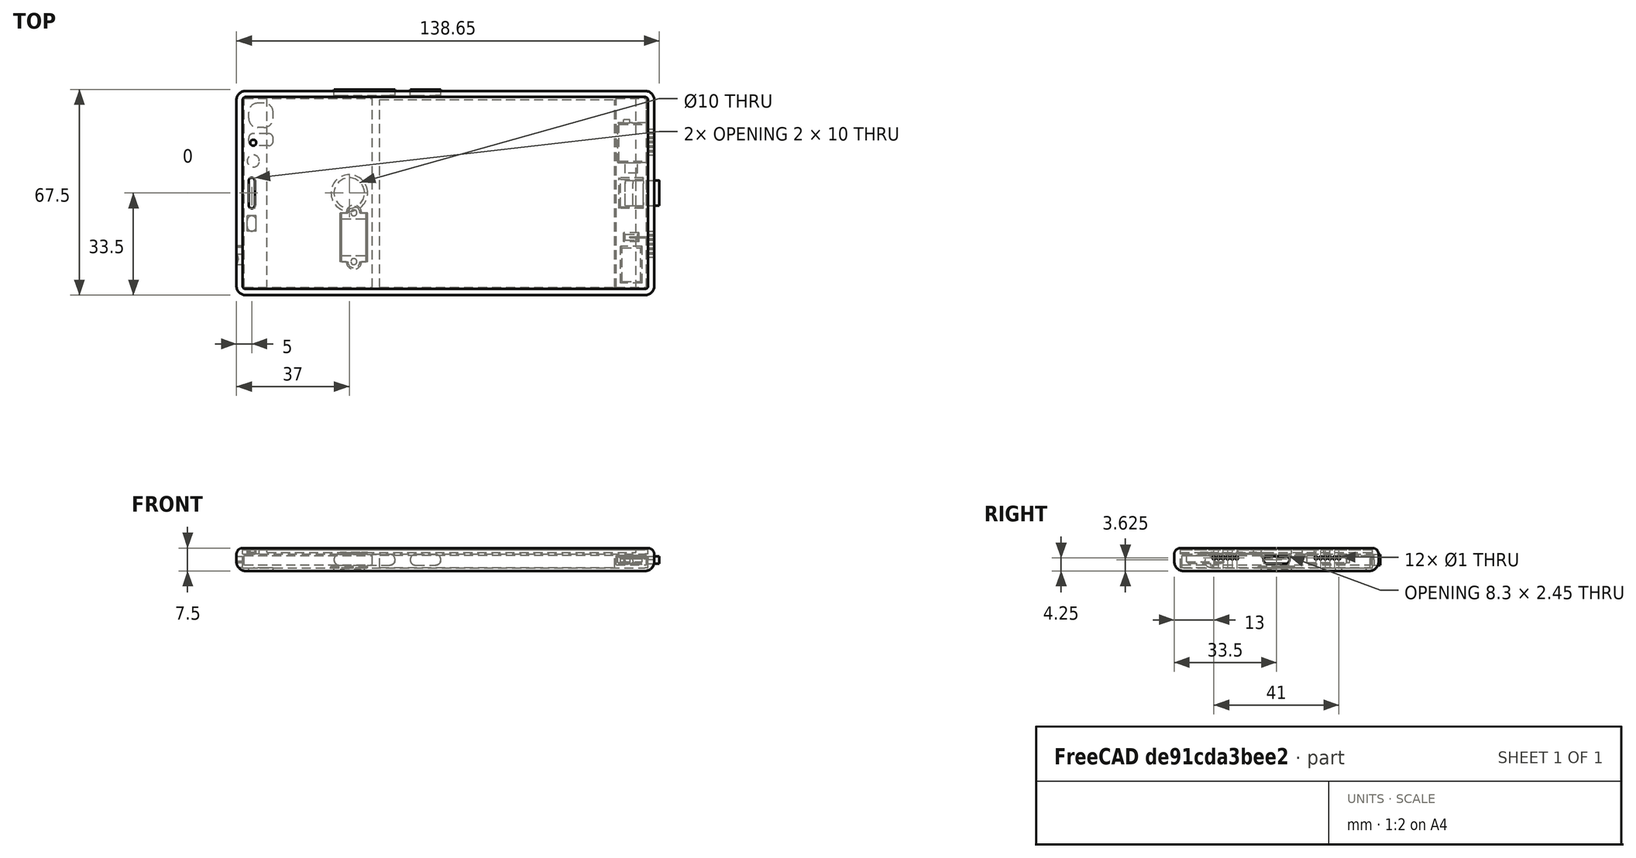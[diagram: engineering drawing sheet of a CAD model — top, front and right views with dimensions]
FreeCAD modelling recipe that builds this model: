
FCSTD DOCUMENT  (FreeCAD 0.16R6706 (Git))
Label: uCromy 2017
License: All rights reserved
LicenseURL: http://en.wikipedia.org/wiki/All_rights_reserved
objects: Part::Cut×45, Part::Box×37, Part::Cylinder×31, Part::Fillet×22, Part::MultiFuse×12, Part::Chamfer×4, Part::Sphere×1
note: 152 computed .brp shape members not serialized (recipe doc carries the construction recipe); baked Part::Feature solids carry a one-line shape summary decoded from their .brp

FEATURE [Part::Box] Box  label="Cubo"
  Height = 7.5
  Length = 137
  Width = 67
FEATURE [Part::Fillet] Fillet
  Base = -> Box
  Edges = 8 edges r=3: [Edge1,Edge3,Edge4,Edge5,Edge7,Edge8,Edge9,Edge11]
FEATURE [Part::Fillet] Fillet001
  Base = -> Fillet
  Edges = 7 edges r=2: [Edge1,Edge5,Edge7,Edge8,Edge9,Edge10,Edge11]
FEATURE [Part::Box] Box001  label="Cubo001"
  Height = 10
  Length = 133
  Placement = pos=(2,2,5.5) rot=(0,0,1;0rad)
  Width = 63
FEATURE [Part::Fillet] Fillet002
  Base = -> Box001
  Edges = 4 edges r=1: [Edge1,Edge3,Edge5,Edge7]
  Placement = pos=(0,0,-4.5) rot=(0,0,1;0rad)
FEATURE [Part::Cut] Cut  label="Chassis"
  Base = -> Fillet001
  Tool = -> Fillet002
FEATURE [Part::Box] Box003  label="Cubo003"
  Height = 0.5
  Length = 133
  Placement = pos=(2,2,5.5) rot=(0,0,1;0rad)
  Width = 63
FEATURE [Part::Fillet] Fillet004  label="Dont show001"
  Base = -> Box003
  Edges = 4 edges r=1: [Edge1,Edge3,Edge5,Edge7]
FEATURE [Part::Box] Box004  label="Cubo004"
  Height = 0.5
  Length = 133
  Placement = pos=(2,2,5.5) rot=(0,0,1;0rad)
  Width = 63
FEATURE [Part::Fillet] Fillet005  label="Touchscreen"
  Base = -> Box004
  Edges = 4 edges r=1: [Edge1,Edge3,Edge5,Edge7]
  Placement = pos=(0,0,1.5) rot=(0,0,1;0rad)
FEATURE [Part::Box] Box005  label="Screen"
  Height = 1
  Length = 121
  Placement = pos=(10,2,6) rot=(0,0,1;0rad)
  Width = 63
FEATURE [Part::Box] Box006  label="Screen001"
  Height = 1
  Length = 8
  Placement = pos=(2,2,6) rot=(0,0,1;0rad)
  Width = 63
FEATURE [Part::Box] Box007  label="Screen002"
  Height = 1
  Length = 4
  Placement = pos=(131,2,6) rot=(0,0,1;0rad)
  Width = 63
FEATURE [Part::Fillet] Fillet006  label="Bottom"
  Base = -> Box007
  Edges = 2 edges r=1: [Edge5,Edge7]
FEATURE [Part::Fillet] Fillet007  label="Top"
  Base = -> Box006
  Edges = 2 edges r=1: [Edge1,Edge3]
FEATURE [Part::Box] Box008  label="Cubo005"
  Height = 0.2
  Length = 8
  Placement = pos=(35,10.5,1) rot=(0,0,1;0rad)
  Width = 16
FEATURE [Part::Cylinder] Cylinder  label="Cilindro"
  Angle = 360
  Height = 0.2
  Placement = pos=(39,10.5,1) rot=(0,0,1;0rad)
  Radius = 2
FEATURE [Part::Cylinder] Cylinder001  label="Cilindro001"
  Angle = 360
  Height = 0.2
  Placement = pos=(39,26.5,1) rot=(0,0,1;0rad)
  Radius = 2
FEATURE [Part::MultiFuse] Fusion  label="Chapa flex pantalla"
  Placement = pos=(-0.5,0.5,4.8) rot=(0,0,1;0rad)
  Shapes = -> [Box008,Cylinder001,Cylinder]
FEATURE [Part::Box] Box009  label="Cubo006"
  Height = 0.3
  Length = 9
  Placement = pos=(34,11,1) rot=(0,0,1;0rad)
  Width = 16
FEATURE [Part::Cylinder] Cylinder002  label="Cilindro002"
  Angle = 360
  Height = 0.3
  Placement = pos=(38.5,11,1) rot=(0,0,1;0rad)
  Radius = 2.5
FEATURE [Part::Cylinder] Cylinder003  label="Cilindro003"
  Angle = 360
  Height = 0.3
  Placement = pos=(38.5,27,1) rot=(0,0,1;0rad)
  Radius = 2.5
FEATURE [Part::MultiFuse] Fusion001  label="Agujero flex pantalla"
  Placement = pos=(0,0,4.4) rot=(0,0,1;0rad)
  Shapes = -> [Box009,Cylinder003,Cylinder002]
FEATURE [Part::Box] Box010  label="Cubo007"
  Height = 1.2
  Length = 8
  Placement = pos=(34.5,11,5) rot=(0,0,1;0rad)
  Width = 16
FEATURE [Part::Cylinder] Cylinder004  label="Cilindro004"
  Angle = 360
  Height = 10
  Placement = pos=(38.5,27,1) rot=(0,0,1;0rad)
  Radius = 1
FEATURE [Part::Cylinder] Cylinder005  label="Cilindro005"
  Angle = 360
  Height = 10
  Placement = pos=(38.5,11,1) rot=(0,0,1;0rad)
  Radius = 1
FEATURE [Part::Cut] Cut001
  Base = -> Box010
  Tool = -> Cylinder004
FEATURE [Part::Cut] Cut002
  Base = -> Cut001
  Tool = -> Cylinder005
FEATURE [Part::Cut] Cut003
  Base = -> Fusion001
  Tool = -> Cylinder005
FEATURE [Part::Cut] Cut004
  Base = -> Cut003
  Placement = pos=(0,0,0.4) rot=(0,0,1;0rad)
  Tool = -> Cylinder004
FEATURE [Part::Cut] Cut005
  Base = -> Fusion
  Tool = -> Cylinder004
FEATURE [Part::Cut] Cut006  label="Chapa flex"
  Base = -> Cut005
  Tool = -> Cylinder005
FEATURE [Part::Cylinder] Cylinder006  label="Cilindro006"
  Angle = 360
  Height = 10
  Placement = pos=(38.5,11,1) rot=(0,0,1;0rad)
  Radius = 1.5
FEATURE [Part::Cylinder] Cylinder007  label="Cilindro007"
  Angle = 360
  Height = 10
  Placement = pos=(38.5,27,1) rot=(0,0,1;0rad)
  Radius = 1.5
FEATURE [Part::Cut] Cut007
  Base = -> Cut002
  Tool = -> Cylinder007
FEATURE [Part::Cut] Cut008
  Base = -> Cut007
  Tool = -> Cylinder006
FEATURE [Part::MultiFuse] Fusion002  label="Dont show"
  Shapes = -> [Cut004,Cut008]
FEATURE [Part::Cut] Cut009
  Base = -> Fillet004
  Tool = -> Fusion002
FEATURE [Part::Box] Box011  label="Cubo008"
  Height = 0.3
  Length = 9
  Placement = pos=(34,11,5.5) rot=(0,0,1;0rad)
  Width = 2
FEATURE [Part::Box] Box012  label="Cubo009"
  Height = 0.3
  Length = 9
  Placement = pos=(34,25,5.5) rot=(0,0,1;0rad)
  Width = 2
FEATURE [Part::MultiFuse] Fusion003
  Shapes = -> [Cut009,Box011,Box012]
FEATURE [Part::Cylinder] Cylinder008  label="Cilindro008"
  Angle = 360
  Height = 0.1
  Placement = pos=(38.5,11,1) rot=(0,0,1;0rad)
  Radius = 1.2
FEATURE [Part::Cylinder] Cylinder009  label="Cilindro009"
  Angle = 360
  Height = 0.1
  Placement = pos=(38.5,27,1) rot=(0,0,1;0rad)
  Radius = 1.2
FEATURE [Part::Cut] Cut010
  Base = -> Fusion003
  Tool = -> Cylinder008
FEATURE [Part::Cut] Cut011
  Base = -> Cut010
  Tool = -> Cylinder009
FEATURE [Part::Cut] Cut012
  Base = -> Cut011
  Tool = -> Cylinder004
FEATURE [Part::Cut] Cut013
  Base = -> Cut012
  Tool = -> Cylinder005
FEATURE [Part::Box] Box013  label="PCB"
  Height = 3
  Length = 42
  Placement = pos=(2.5,2.5,2) rot=(0,0,1;0rad)
  Width = 62
FEATURE [Part::Box] Box014  label="Loud_Speaker"
  Height = 3
  Length = 10
  Placement = pos=(124.5,2.5,2) rot=(0,0,1;0rad)
  Width = 62
FEATURE [Part::Box] Box015  label="Battery"
  Height = 4.05
  Length = 77
  Placement = pos=(47,2.5,1.1) rot=(0,0,1;0rad)
  Width = 61.7
FEATURE [Part::Box] Box016  label="Cubo010"
  Height = 10
  Length = 2
  Placement = pos=(4,28.5,0) rot=(0,0,1;0rad)
  Width = 10
FEATURE [Part::Fillet] Fillet008
  Base = -> Box016
  Edges = 4 edges r=0.95: [Edge1,Edge3,Edge5,Edge7]
FEATURE [Part::Cut] Cut014
  Base = -> Fillet005
  Tool = -> Fillet008
FEATURE [Part::Cut] Cut015
  Base = -> Fillet007
  Tool = -> Fillet008
FEATURE [Part::Cylinder] Cylinder010  label="Cilindro010"
  Angle = 360
  Height = 10
  Placement = pos=(5.5,50,0) rot=(0,0,1;0rad)
  Radius = 1
FEATURE [Part::Cut] Cut016
  Base = -> Cut014
  Tool = -> Cylinder010
FEATURE [Part::Cut] Cut017
  Base = -> Cut013
  Tool = -> Cylinder010
FEATURE [Part::Cylinder] Cylinder011  label="Cilindro011"
  Angle = 360
  Height = 10
  Placement = pos=(5.5,44,0) rot=(0,0,1;0rad)
  Radius = 2
FEATURE [Part::Box] Box017  label="Cubo011"
  Height = 10
  Length = 3
  Placement = pos=(3.5,21,0) rot=(0,0,1;0rad)
  Width = 5
FEATURE [Part::Cylinder] Cylinder012  label="Cilindro012"
  Angle = 360
  Height = 2
  Placement = pos=(5.5,50,5.5) rot=(0,0,1;0rad)
  Radius = 1
FEATURE [Part::Cut] Cut018
  Base = -> Cut015
  Tool = -> Cylinder010
FEATURE [Part::Cut] Cut019
  Base = -> Cut017
  Tool = -> Cylinder011
FEATURE [Part::Cut] Cut020
  Base = -> Cut019
  Tool = -> Box017
FEATURE [Part::Box] Box018  label="Cubo012"
  Height = 10
  Length = 3
  Placement = pos=(3.5,21,0) rot=(0,0,1;0rad)
  Width = 5
FEATURE [Part::Fillet] Fillet009
  Base = -> Box018
  Edges = 4 edges r=1.49: [Edge1,Edge3,Edge5,Edge7]
FEATURE [Part::Cut] Cut021
  Base = -> Cut018
  Tool = -> Fillet009
FEATURE [Part::Cut] Cut022
  Base = -> Cut020
  Tool = -> Fillet008
FEATURE [Part::Cut] Cut023
  Base = -> Cut021
  Tool = -> Cylinder011
FEATURE [Part::Box] Box019  label="Cubo013"
  Height = 10
  Length = 8
  Placement = pos=(4,55,-1) rot=(0,0,1;0rad)
  Width = 8
FEATURE [Part::Fillet] Fillet010
  Base = -> Box019
  Edges = 4 edges r=3: [Edge1,Edge3,Edge5,Edge7]
FEATURE [Part::Box] Box020  label="Cubo014"
  Height = 1
  Length = 8
  Placement = pos=(4,55,-1) rot=(0,0,1;0rad)
  Width = 8
FEATURE [Part::Fillet] Fillet011  label="Lente Cámara"
  Base = -> Box020
  Edges = 4 edges r=3: [Edge1,Edge3,Edge5,Edge7]
  Placement = pos=(0,0,1) rot=(0,0,1;0rad)
FEATURE [Part::Box] Box021  label="Cubo015"
  Height = 10
  Length = 8
  Placement = pos=(4,55,-1) rot=(0,0,1;0rad)
  Width = 4
FEATURE [Part::Fillet] Fillet012
  Base = -> Box021
  Edges = 4 edges r=1.5: [Edge1,Edge3,Edge5,Edge7]
  Placement = pos=(0,-6,0) rot=(0,0,1;0rad)
FEATURE [Part::Cut] Cut024
  Base = -> Cut
  Tool = -> Fillet010
FEATURE [Part::Box] Box022  label="Cubo016"
  Height = 1
  Length = 8
  Placement = pos=(4,55,-1) rot=(0,0,1;0rad)
  Width = 4
FEATURE [Part::Fillet] Fillet013  label="Lente Flash"
  Base = -> Box022
  Edges = 4 edges r=1.5: [Edge1,Edge3,Edge5,Edge7]
  Placement = pos=(0,-6,1) rot=(0,0,1;0rad)
FEATURE [Part::Cut] Cut025
  Base = -> Cut024
  Tool = -> Fillet012
FEATURE [Part::MultiFuse] Fusion004
  Shapes = -> [Cut023,Cut022,Fillet006]
FEATURE [Part::Cylinder] Cylinder013  label="Cilindro013"
  Angle = 360
  Height = 10
  Placement = pos=(130,54,4.25) rot=(0.57735,0.57735,0.57735;2.0944rad)
  Radius = 0.5
FEATURE [Part::Cylinder] Cylinder014  label="Cilindro014"
  Angle = 360
  Height = 10
  Placement = pos=(130,51,4.25) rot=(0.57735,0.57735,0.57735;2.0944rad)
  Radius = 0.5
FEATURE [Part::Cylinder] Cylinder015  label="Cilindro015"
  Angle = 360
  Height = 10
  Placement = pos=(130,52.5,4.25) rot=(0.57735,0.57735,0.57735;2.0944rad)
  Radius = 0.5
FEATURE [Part::MultiFuse] Fusion005
  Shapes = -> [Cylinder013,Cylinder015,Cylinder014]
FEATURE [Part::Cylinder] Cylinder016  label="Cilindro016"
  Angle = 360
  Height = 10
  Placement = pos=(130,54,4.25) rot=(0.57735,0.57735,0.57735;2.0944rad)
  Radius = 0.5
FEATURE [Part::Cylinder] Cylinder017  label="Cilindro017"
  Angle = 360
  Height = 10
  Placement = pos=(130,51,4.25) rot=(0.57735,0.57735,0.57735;2.0944rad)
  Radius = 0.5
FEATURE [Part::Cylinder] Cylinder018  label="Cilindro018"
  Angle = 360
  Height = 10
  Placement = pos=(130,52.5,4.25) rot=(0.57735,0.57735,0.57735;2.0944rad)
  Radius = 0.5
FEATURE [Part::MultiFuse] Fusion006
  Placement = pos=(0,-4.5,0) rot=(0,0,1;0rad)
  Shapes = -> [Cylinder016,Cylinder018,Cylinder017]
FEATURE [Part::MultiFuse] Fusion007  label="Agujero altavoz"
  Shapes = -> [Fusion005,Fusion006]
FEATURE [Part::Cylinder] Cylinder021  label="Cilindro021"
  Angle = 360
  Height = 10
  Placement = pos=(130,52.5,4.25) rot=(0.57735,0.57735,0.57735;2.0944rad)
  Radius = 0.5
FEATURE [Part::Cylinder] Cylinder020  label="Cilindro020"
  Angle = 360
  Height = 10
  Placement = pos=(130,51,4.25) rot=(0.57735,0.57735,0.57735;2.0944rad)
  Radius = 0.5
FEATURE [Part::Cylinder] Cylinder019  label="Cilindro019"
  Angle = 360
  Height = 10
  Placement = pos=(130,54,4.25) rot=(0.57735,0.57735,0.57735;2.0944rad)
  Radius = 0.5
FEATURE [Part::MultiFuse] Fusion008  label="Fusion007"
  Placement = pos=(0,-38,0) rot=(0,0,1;0rad)
  Shapes = -> [Cylinder019,Cylinder021,Cylinder020]
FEATURE [Part::Cylinder] Cylinder022  label="Cilindro022"
  Angle = 360
  Height = 10
  Placement = pos=(130,52.5,4.25) rot=(0.57735,0.57735,0.57735;2.0944rad)
  Radius = 0.5
FEATURE [Part::Cylinder] Cylinder023  label="Cilindro023"
  Angle = 360
  Height = 10
  Placement = pos=(130,51,4.25) rot=(0.57735,0.57735,0.57735;2.0944rad)
  Radius = 0.5
FEATURE [Part::Cylinder] Cylinder024  label="Cilindro024"
  Angle = 360
  Height = 10
  Placement = pos=(130,54,4.25) rot=(0.57735,0.57735,0.57735;2.0944rad)
  Radius = 0.5
FEATURE [Part::MultiFuse] Fusion009  label="Fusion008"
  Placement = pos=(0,-33.5,0) rot=(0,0,1;0rad)
  Shapes = -> [Cylinder024,Cylinder022,Cylinder023]
FEATURE [Part::MultiFuse] Fusion010  label="Agujero Micro"
  Shapes = -> [Fusion008,Fusion009]
FEATURE [Part::Cut] Cut026
  Base = -> Cut025
  Tool = -> Fusion007
FEATURE [Part::Cut] Cut027
  Base = -> Cut026
  Tool = -> Fusion010
FEATURE [Part::Box] Box023  label="Cubo017"
  Height = 2.45
  Length = 6.65
  Width = 8.3
FEATURE [Part::Fillet] Fillet014  label="USB-C"
  Base = -> Box023
  Edges = 4 edges r=1: [Edge9,Edge10,Edge11,Edge12]
  Placement = pos=(132,29.35,2.4) rot=(0,0,1;0rad)
FEATURE [Part::Cut] Cut028
  Base = -> Cut027
  Tool = -> Fillet014
FEATURE [Part::Box] Box024  label="Cubo018"
  Height = 2.45
  Length = 8.65
  Width = 8.3
FEATURE [Part::Fillet] Fillet015  label="USB-C001"
  Base = -> Box024
  Edges = 4 edges r=1: [Edge9,Edge10,Edge11,Edge12]
  Placement = pos=(130,29.35,2.4) rot=(0,0,1;0rad)
FEATURE [Part::Cylinder] Cylinder026  label="phones"
  Angle = 360
  Height = 10
  Placement = pos=(-2,11.75,3) rot=(0.57735,0.57735,0.57735;2.0944rad)
  Radius = 1.75
FEATURE [Part::Cut] Cut029
  Base = -> Cut028
  Tool = -> Cylinder026
FEATURE [Part::Box] Box026  label="Agujero Altavoz"
  Height = 3
  Length = 10
  Placement = pos=(125,43.5,2.2) rot=(0,0,1;0rad)
  Width = 13
FEATURE [Part::Cut] Cut030
  Base = -> Box014
  Tool = -> Box026
FEATURE [Part::Cylinder] Cylinder027  label="Cilindro025"
  Angle = 360
  Height = 10
  Placement = pos=(0,16,3) rot=(0.57735,0.57735,0.57735;2.0944rad)
  Radius = 0.25
FEATURE [Part::Cylinder] Cylinder028  label="Cilindro026"
  Angle = 360
  Height = 10
  Placement = pos=(129,19,4.25) rot=(0.57735,0.57735,0.57735;2.0944rad)
  Radius = 0.25
FEATURE [Part::Cut] Cut031
  Base = -> Cut029
  Tool = -> Cylinder027
FEATURE [Part::Cut] Cut032
  Base = -> Cut030
  Tool = -> Cylinder028
FEATURE [Part::Box] Box027  label="Cubo021"
  Height = 2.45
  Length = 8.65
  Width = 8.3
FEATURE [Part::Fillet] Fillet016  label="USB-C002"
  Base = -> Box027
  Edges = 4 edges r=1: [Edge9,Edge10,Edge11,Edge12]
  Placement = pos=(127.5,29.35,2.4) rot=(0,0,1;0rad)
FEATURE [Part::Cut] Cut033
  Base = -> Cut032
  Tool = -> Fillet015
FEATURE [Part::Cylinder] Cylinder029  label="Cilindro027"
  Angle = 360
  Height = 10
  Placement = pos=(37,33.5,-1) rot=(0,0,1;0rad)
  Radius = 5
FEATURE [Part::Cylinder] Cylinder030  label="Cilindro028"
  Angle = 360
  Height = 1
  Placement = pos=(37,33.5,0) rot=(0,0,1;0rad)
  Radius = 5
FEATURE [Part::Cut] Cut034
  Base = -> Cut031
  Tool = -> Cylinder029
FEATURE [Part::Cylinder] Cylinder031  label="Cilindro029"
  Angle = 360
  Height = 0.5
  Placement = pos=(37,33.5,1) rot=(0,0,1;0rad)
  Radius = 6
FEATURE [Part::Sphere] Sphere  label="Esfera"
  Angle1 = 70
  Angle2 = 90
  Angle3 = 360
  Placement = pos=(37,33.5,-14.25) rot=(0,0,1;0rad)
  Radius = 15
FEATURE [Part::Cut] Cut035
  Base = -> Cylinder030
  Tool = -> Sphere
FEATURE [Part::Fillet] Fillet017
  Base = -> Cut035
  Edges = 1 edges: [Edge4 r1=1 r2=2]
FEATURE [Part::MultiFuse] Fusion011  label="Sensor de huellas"
  Shapes = -> [Fillet017,Cylinder031]
FEATURE [Part::Box] Box028  label="Cubo022"
  Height = 3.5
  Length = 10
  Placement = pos=(57,60,2.5) rot=(0,0,1;0rad)
  Width = 10
FEATURE [Part::Fillet] Fillet018
  Base = -> Box028
  Edges = 4 edges r=1.7: [Edge2,Edge4,Edge6,Edge8]
  Placement = pos=(0,0,-0.6) rot=(0,0,1;0rad)
FEATURE [Part::Box] Box029  label="Cubo023"
  Height = 3.5
  Length = 20
  Placement = pos=(57,60,2.5) rot=(0,0,1;0rad)
  Width = 10
FEATURE [Part::Fillet] Fillet019
  Base = -> Box029
  Edges = 4 edges r=1.7: [Edge2,Edge4,Edge6,Edge8]
  Placement = pos=(-25,0,-0.6) rot=(0,0,1;0rad)
FEATURE [Part::Box] Box030  label="Cubo024"
  Height = 3.5
  Length = 10
  Placement = pos=(57,60,2.5) rot=(0,0,1;0rad)
  Width = 2
FEATURE [Part::Fillet] Fillet020  label="PowerButton"
  Base = -> Box030
  Edges = 4 edges r=1.7: [Edge2,Edge4,Edge6,Edge8]
  Placement = pos=(0,5.5,-0.6) rot=(0,0,1;0rad)
FEATURE [Part::Box] Box031  label="Cubo025"
  Height = 3.5
  Length = 20
  Placement = pos=(57,60,2.5) rot=(0,0,1;0rad)
  Width = 2
FEATURE [Part::Fillet] Fillet021  label="VolumeButton"
  Base = -> Box031
  Edges = 4 edges r=1.7: [Edge2,Edge4,Edge6,Edge8]
  Placement = pos=(-25,5.5,-0.6) rot=(0,0,1;0rad)
FEATURE [Part::Cut] Cut036
  Base = -> Cut034
  Tool = -> Fillet019
FEATURE [Part::Cut] Cut037
  Base = -> Cut036
  Tool = -> Fillet018
FEATURE [Part::Box] Box032  label="Cubo026"
  Height = 10
  Length = 5
  Placement = pos=(124,14,0) rot=(0,0,1;0rad)
  Width = 3
FEATURE [Part::Chamfer] Chamfer
  Base = -> Box032
  Edges = 4 edges r=0.5: [Edge4,Edge8,Edge9,Edge11]
  Placement = pos=(3,3.5,4.2) rot=(0,0,1;0rad)
FEATURE [Part::Cut] Cut038
  Base = -> Cut033
  Tool = -> Chamfer
FEATURE [Part::Box] Box033  label="Cubo027"
  Height = 10
  Length = 8
  Placement = pos=(124,28.5,0) rot=(0,0,1;0rad)
  Width = 10
FEATURE [Part::Chamfer] Chamfer001
  Base = -> Box033
  Edges = 4 edges r=0.5: [Edge4,Edge8,Edge9,Edge11]
  Placement = pos=(1.5,0,4) rot=(0,0,1;0rad)
FEATURE [Part::Cut] Cut039
  Base = -> Cut038
  Tool = -> Chamfer001
FEATURE [Part::Box] Box034  label="Cubo028"
  Height = 3
  Length = 7
  Placement = pos=(126,4,2.5) rot=(0,0,1;0rad)
  Width = 12
FEATURE [Part::Chamfer] Chamfer002
  Base = -> Box034
  Edges = 4 edges r=0.5: [Edge4,Edge8,Edge9,Edge11]
FEATURE [Part::Cut] Cut040
  Base = -> Cut039
  Tool = -> Chamfer002
FEATURE [Part::Box] Box035  label="Cubo029"
  Height = 2.45
  Length = 8.65
  Width = 8.3
FEATURE [Part::Fillet] Fillet022  label="USB-C003"
  Base = -> Box035
  Edges = 4 edges r=1: [Edge9,Edge10,Edge11,Edge12]
  Placement = pos=(130,29.35,2.4) rot=(0,0,1;0rad)
FEATURE [Part::Cut] Cut041
  Base = -> Cut040
  Tool = -> Fillet016
FEATURE [Part::Box] Box036  label="Cubo030"
  Height = 10
  Length = 2
  Placement = pos=(127,55,2.75) rot=(0,0,1;0rad)
  Width = 2.5
FEATURE [Part::Chamfer] Chamfer003
  Base = -> Cut041
  Edges = 3 edges r=0.5: [Edge41,Edge44,Edge45]
FEATURE [Part::Cut] Cut042
  Base = -> Chamfer003
  Tool = -> Box036
FEATURE [Part::Box] Box037  label="Cubo031"
  Height = 10
  Length = 3
  Placement = pos=(128,41,4.75) rot=(0,0,1;0rad)
  Width = 6
FEATURE [Part::Cut] Cut043
  Base = -> Cut042
  Tool = -> Box037
FEATURE [Part::Box] Box038  label="Cubo032"
  Height = 10
  Length = 4
  Placement = pos=(127.5,40,4.75) rot=(0,0,1;0rad)
  Width = 4
FEATURE [Part::Cut] Cut044
  Base = -> Cut043
  Tool = -> Box038
